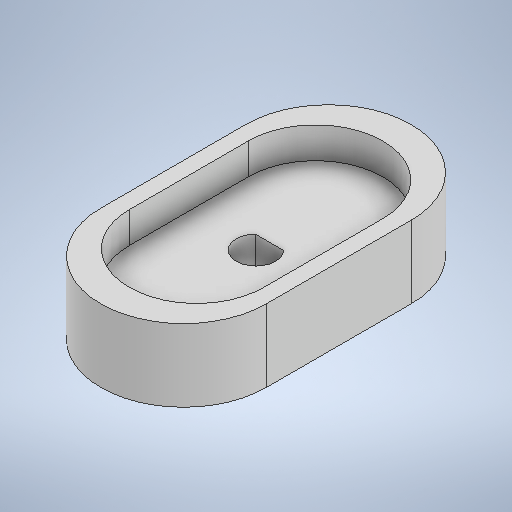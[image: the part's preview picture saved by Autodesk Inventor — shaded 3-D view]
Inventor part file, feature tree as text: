
AUTODESK INVENTOR PART (.ipt)
format: ipt  version: 2025.2 (Build 292293000, 293)  size: 242,176 bytes
history: native  units: in
note: dims shown in document units (in); Inventor stores cm internally (conversion verified against a paired STEP export)
features: extrude x3, sketch x3
ambient origin geometry x8: Origin, YZ Plane, XZ Plane, XY Plane, X Axis, Y Axis, Z Axis, Center Point
bodies: Solid1 (feature_tree)
feature tree (6):
  extrude  "Extrusion1"  Depth=0.2756in
  extrude  "Extrusion2"  Depth=0.1181in TaperAngle=0.0deg
  extrude  "Extrusion3"  Depth=0.0512in
  sketch  "Sketch1"  dims[d4=0.6299in d5=1.1811in d6=0.2756in d7=0.0in d11=0.9646in]
  sketch  "Sketch4"  dims[d12=0.5118in d13=0.1181in d14=0.0in]
  sketch  "Sketch5"  dims[d15=0.1496in d16=0.0512in d17=0.7087in d18=0.0in d22=0.0197in d23=0.0344in d24=0.0197in d25=0.0344in]
